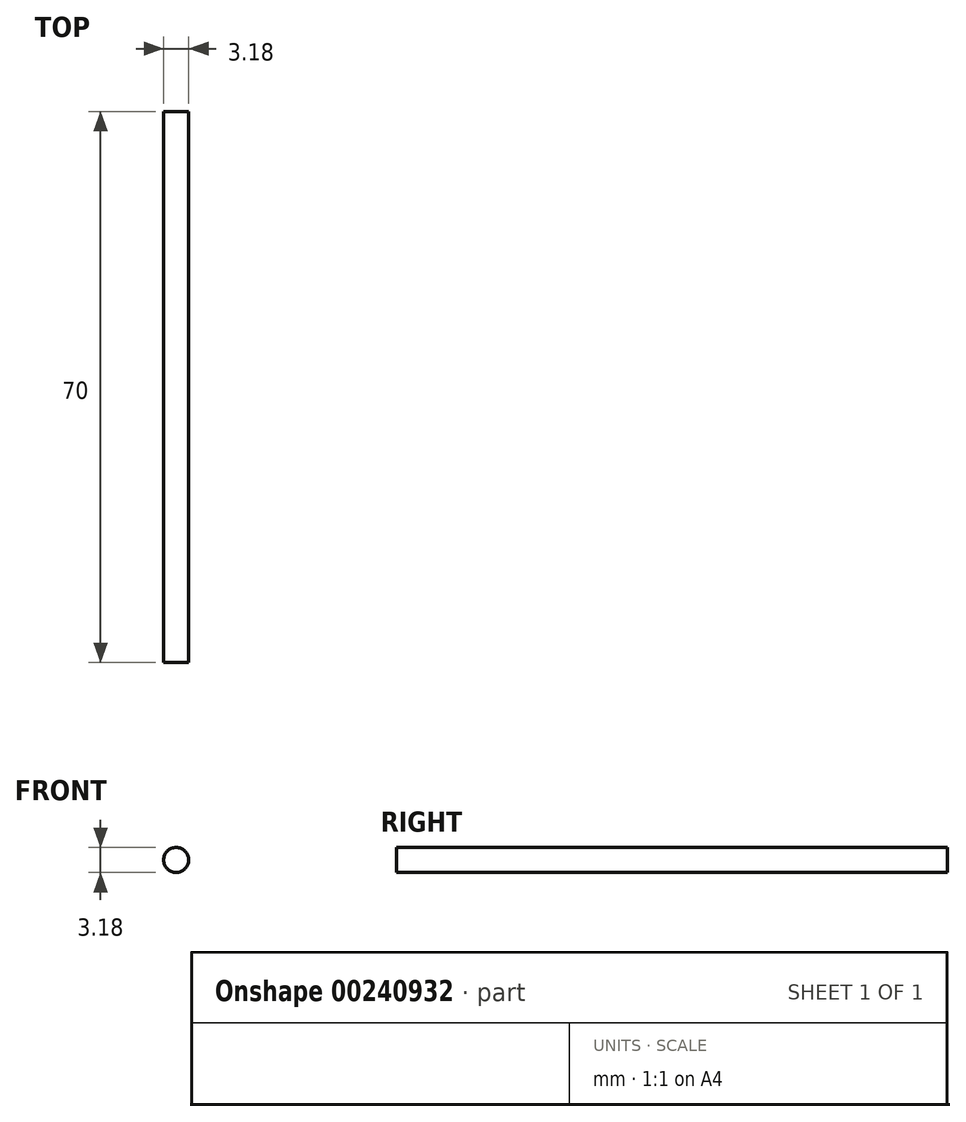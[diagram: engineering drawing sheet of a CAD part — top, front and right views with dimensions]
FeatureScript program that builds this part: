
annotation { "Feature Type Name" : "Feature", "Feature Type Description" : "" }
export const myFeature = defineFeature(function(context is Context, id is Id, definition is map)
    precondition{}
    {
        {
            var Q0;
            Q0=qCreatedBy(makeId("Front.planeOp"),FACE);
            var sketch = newSketch(context, id + "F0", { "sketchPlane" : qUnion([Q0])});
            skCircle(sketch, "E0", {"center": v(0, 0) * mm, "radius": 1.59 * mm});
            skSolve(sketch);
        }
        {
            var Q0;
            Q0 = qSketchRegion(id + "F0", true);
            extrude(context, id + "F1", {"entities" : qUnion([Q0]), "depth" : 70 * mm});
        }
    });
